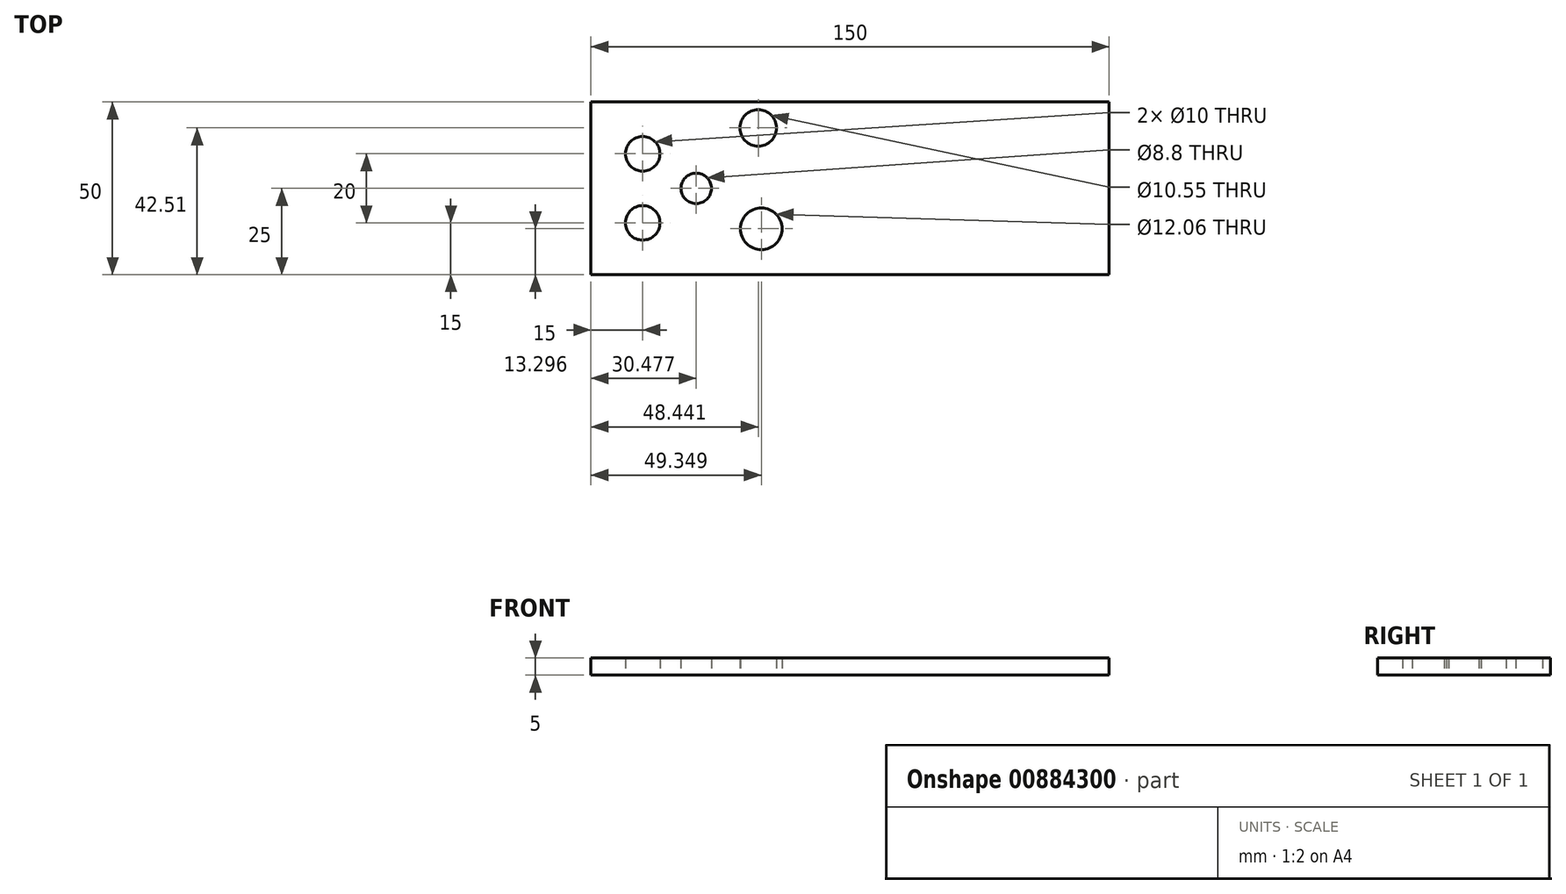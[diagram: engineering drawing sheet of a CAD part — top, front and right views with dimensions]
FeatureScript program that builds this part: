
annotation { "Feature Type Name" : "Feature", "Feature Type Description" : "" }
export const myFeature = defineFeature(function(context is Context, id is Id, definition is map)
    precondition{}
    {
        {
            var Q0;
            Q0=qCreatedBy(makeId("Top.planeOp"),FACE);
            var sketch = newSketch(context, id + "F0", { "sketchPlane" : qUnion([Q0])});
            skLineSegment(sketch, "E0.bottom", {"start": v(-75, 25) * mm, "end": v(75, 25) * mm});
            skLineSegment(sketch, "E0.top", {"start": v(-75, -25) * mm, "end": v(75, -25) * mm});
            skLineSegment(sketch, "E0.left", {"start": v(-75, 25) * mm, "end": v(-75, -25) * mm});
            skLineSegment(sketch, "E0.right", {"start": v(75, 25) * mm, "end": v(75, -25) * mm});
            skPoint(sketch, "E0.middle", {"position": v(0, 0) * mm});
            skCircle(sketch, "E1", {"center": v(-60, 10) * mm, "radius": 5 * mm});
            skCircle(sketch, "E2", {"center": v(-60, -10) * mm, "radius": 5 * mm});
            skCircle(sketch, "E3", {"center": v(-44.52, 0) * mm, "radius": 4.4 * mm});
            skCircle(sketch, "E4", {"center": v(-26.56, 17.51) * mm, "radius": 5.27 * mm});
            skCircle(sketch, "E5", {"center": v(-25.65, -11.7) * mm, "radius": 6.03 * mm});
            skSolve(sketch);
        }
        {
            var Q0;
            Q0=makeQuery(id+"F0.imprint","IMPRINT",FACE,{"disambiguationData":[TD([[makeQuery(id+"F0.imprint","IMPRINT",EDGE,{"derivedFrom":sQuery(id+"F0.wireOp",EDGE,"E0.bottom")}),-1.0]])]});
            extrude(context, id + "F1", {"entities" : qUnion([Q0]), "depth" : 5 * mm, "offsetDistance" : 25 * mm});
        }
    });
